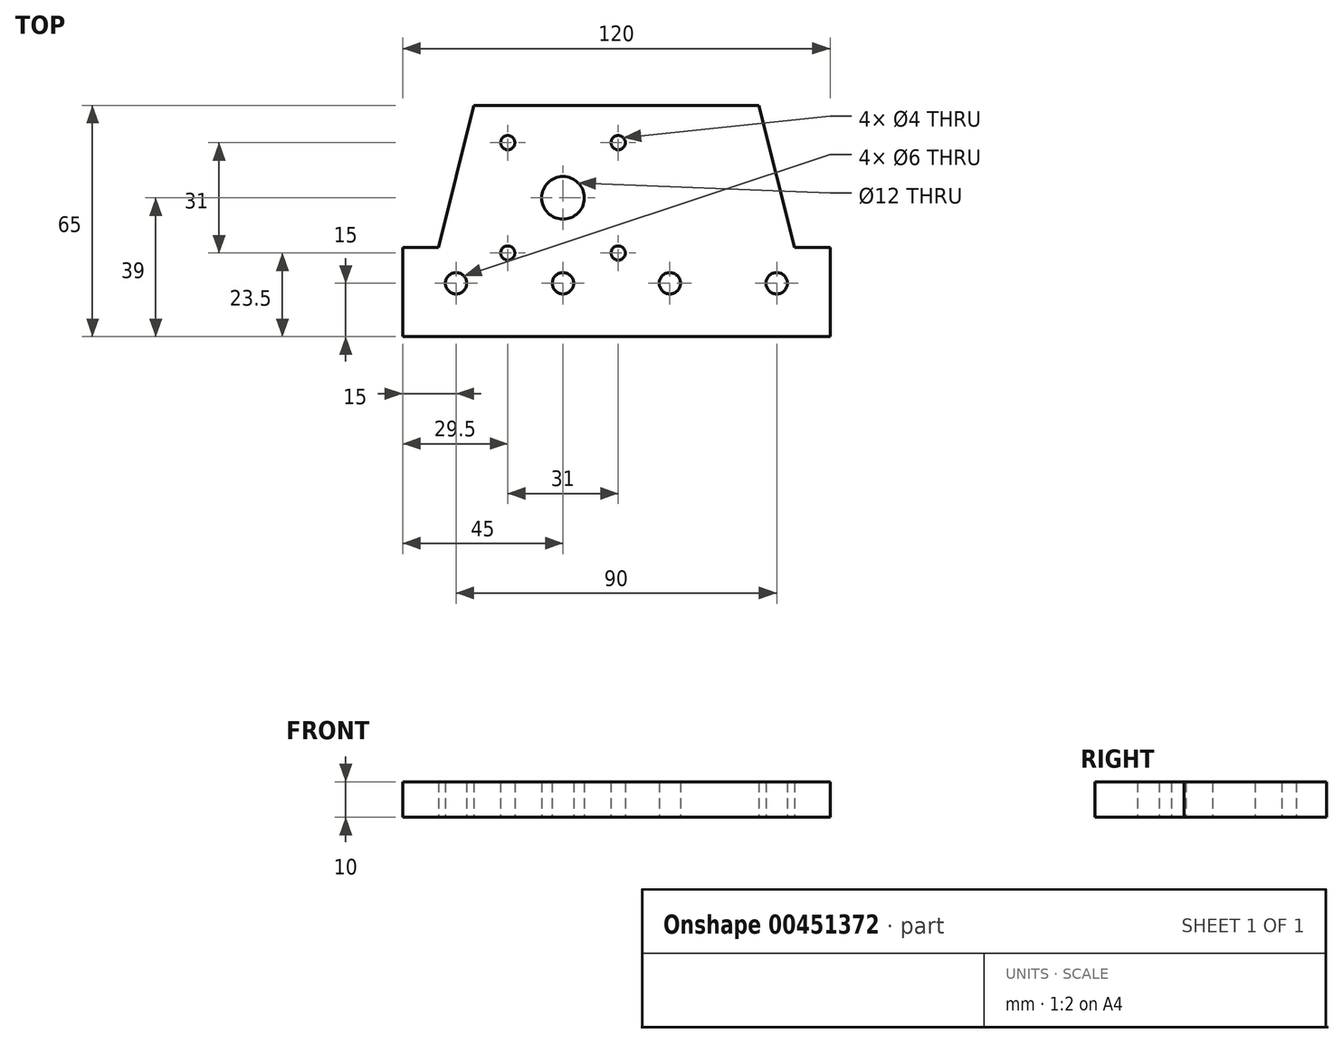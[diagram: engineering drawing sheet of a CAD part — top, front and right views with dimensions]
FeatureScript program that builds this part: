
annotation { "Feature Type Name" : "Feature", "Feature Type Description" : "" }
export const myFeature = defineFeature(function(context is Context, id is Id, definition is map)
    precondition{}
    {
        {
            var Q0;
            Q0=qCreatedBy(makeId("Top.planeOp"),FACE);
            var sketch = newSketch(context, id + "F0", { "sketchPlane" : qUnion([Q0])});
            skLineSegment(sketch, "E0", {"start": v(-60, -65) * mm, "end": v(60, -65) * mm});
            skLineSegment(sketch, "E1", {"start": v(60, -65) * mm, "end": v(60, -40) * mm});
            skLineSegment(sketch, "E2", {"start": v(60, -40) * mm, "end": v(50, -40) * mm});
            skLineSegment(sketch, "E3", {"start": v(50, -40) * mm, "end": v(40, 0) * mm});
            skLineSegment(sketch, "E4", {"start": v(40, 0) * mm, "end": v(-40, 0) * mm});
            skLineSegment(sketch, "E5", {"start": v(-40, 0) * mm, "end": v(-50, -40) * mm});
            skLineSegment(sketch, "E6", {"start": v(-50, -40) * mm, "end": v(-60, -40) * mm});
            skLineSegment(sketch, "E7", {"start": v(-60, -40) * mm, "end": v(-60, -65) * mm});
            skLineSegment(sketch, "E8", {"start": v(-50, -40) * mm, "end": v(-40, -40) * mm, "construction": true});
            skLineSegment(sketch, "E9", {"start": v(-40, -40) * mm, "end": v(-40, 0) * mm, "construction": true});
            skLineSegment(sketch, "E10", {"start": v(50, -40) * mm, "end": v(40, -40) * mm, "construction": true});
            skLineSegment(sketch, "E11", {"start": v(40, -40) * mm, "end": v(40, 0) * mm, "construction": true});
            skLineSegment(sketch, "E12", {"start": v(0, -28.18) * mm, "end": v(-60, -28.18) * mm, "construction": true});
            skSolve(sketch);
        }
        {
            var Q0;
            Q0 = qSketchRegion(id + "F0", true);
            extrude(context, id + "F1", {"entities" : qUnion([Q0]), "depth" : 10 * mm});
        }
        {
            var Q0;
            Q0=qCreatedBy(makeId("Top.planeOp"),FACE);
            var sketch = newSketch(context, id + "F2", { "sketchPlane" : qUnion([Q0])});
            skCircle(sketch, "E13", {"center": v(-15, -26) * mm, "radius": 6 * mm});
            skLineSegment(sketch, "E14.bottom", {"start": v(-36, -5) * mm, "end": v(6, -5) * mm, "construction": true});
            skLineSegment(sketch, "E14.top", {"start": v(-36, -47) * mm, "end": v(6, -47) * mm, "construction": true});
            skLineSegment(sketch, "E14.left", {"start": v(-36, -5) * mm, "end": v(-36, -47) * mm, "construction": true});
            skLineSegment(sketch, "E14.right", {"start": v(6, -5) * mm, "end": v(6, -47) * mm, "construction": true});
            skLineSegment(sketch, "E15", {"start": v(-15, -26) * mm, "end": v(-15, -47) * mm, "construction": true});
            skLineSegment(sketch, "E16", {"start": v(-15, -26) * mm, "end": v(6, -26) * mm, "construction": true});
            skCircle(sketch, "E17", {"center": v(-30.5, -10.5) * mm, "radius": 2 * mm});
            skLineSegment(sketch, "E18", {"start": v(-30.5, -10.5) * mm, "end": v(-36, -10.5) * mm, "construction": true});
            skLineSegment(sketch, "E19", {"start": v(-30.5, -10.5) * mm, "end": v(-30.5, -5) * mm, "construction": true});
            skCircle(sketch, "E20", {"center": v(0.5, -10.5) * mm, "radius": 2 * mm});
            skLineSegment(sketch, "E21", {"start": v(0.5, -10.5) * mm, "end": v(0.5, -5) * mm, "construction": true});
            skLineSegment(sketch, "E22", {"start": v(0.5, -10.5) * mm, "end": v(6, -10.5) * mm, "construction": true});
            skCircle(sketch, "E23", {"center": v(-30.5, -41.5) * mm, "radius": 2 * mm});
            skCircle(sketch, "E24", {"center": v(0.5, -41.5) * mm, "radius": 2 * mm});
            skLineSegment(sketch, "E25", {"start": v(-30.5, -41.5) * mm, "end": v(-36, -41.5) * mm, "construction": true});
            skLineSegment(sketch, "E26", {"start": v(-30.5, -41.5) * mm, "end": v(-30.5, -47) * mm, "construction": true});
            skLineSegment(sketch, "E27", {"start": v(0.5, -41.5) * mm, "end": v(0.5, -47) * mm, "construction": true});
            skLineSegment(sketch, "E28", {"start": v(0.5, -41.5) * mm, "end": v(6, -41.5) * mm, "construction": true});
            skSolve(sketch);
        }
        {
            var Q0;
            Q0 = qSketchRegion(id + "F2", true);
            extrude(context, id + "F3", {"entities" : qUnion([Q0]), "operationType" : NewBodyOperationType.REMOVE, "depth" : 25 * mm});
        }
        {
            var Q0;
            Q0=qCreatedBy(makeId("Top.planeOp"),FACE);
            var sketch = newSketch(context, id + "F4", { "sketchPlane" : qUnion([Q0])});
            skLineSegment(sketch, "E29", {"start": v(-70, -50) * mm, "end": v(70, -50) * mm, "construction": true});
            skCircle(sketch, "E30", {"center": v(-45, -50) * mm, "radius": 3 * mm});
            skCircle(sketch, "E31", {"center": v(-15, -50) * mm, "radius": 3 * mm});
            skCircle(sketch, "E32", {"center": v(45, -50) * mm, "radius": 3 * mm});
            skCircle(sketch, "E33", {"center": v(15, -50) * mm, "radius": 3 * mm});
            skSolve(sketch);
        }
        {
            var Q0;
            Q0 = qSketchRegion(id + "F4", true);
            extrude(context, id + "F5", {"entities" : qUnion([Q0]), "operationType" : NewBodyOperationType.REMOVE, "depth" : 24.5 * mm});
        }
    });
